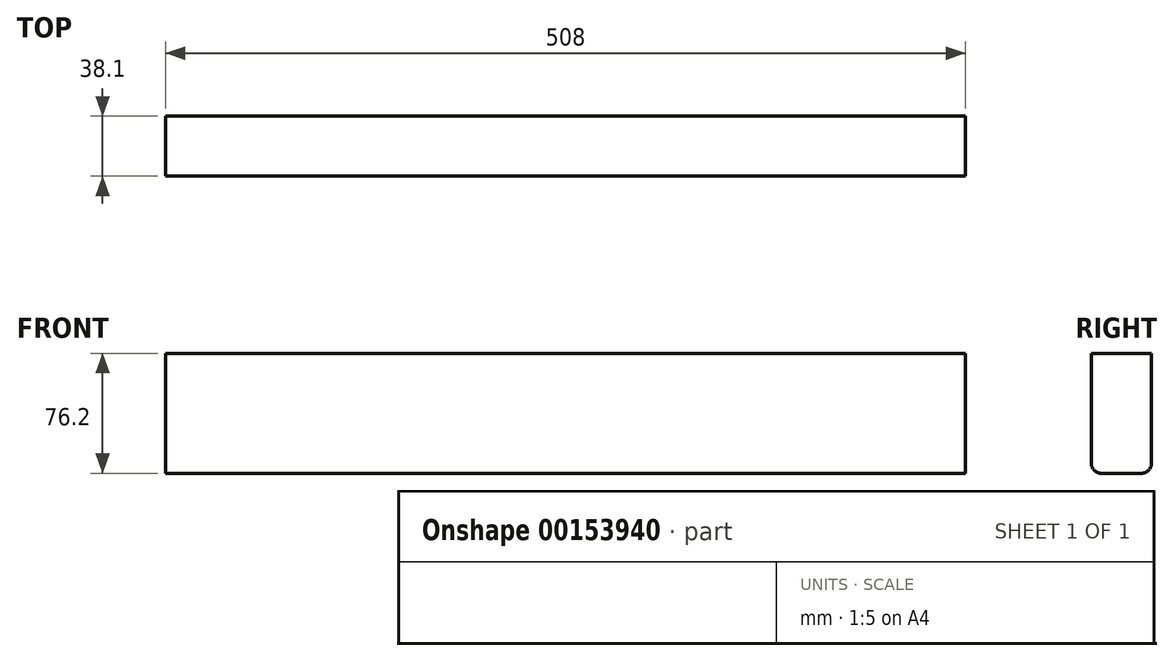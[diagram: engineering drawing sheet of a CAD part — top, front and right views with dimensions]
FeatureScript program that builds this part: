
annotation { "Feature Type Name" : "Feature", "Feature Type Description" : "" }
export const myFeature = defineFeature(function(context is Context, id is Id, definition is map)
    precondition{}
    {
        {
            var Q0;
            Q0=qCreatedBy(makeId("Right.planeOp"),FACE);
            var sketch = newSketch(context, id + "F0", { "sketchPlane" : qUnion([Q0])});
            skLineSegment(sketch, "E0.bottom", {"start": v(31.75, 0) * mm, "end": v(6.35, 0) * mm});
            skLineSegment(sketch, "E0.top", {"start": v(38.1, 76.2) * mm, "end": v(0, 76.2) * mm});
            skLineSegment(sketch, "E0.left", {"start": v(38.1, 6.35) * mm, "end": v(38.1, 76.2) * mm});
            skLineSegment(sketch, "E0.right", {"start": v(0, 6.35) * mm, "end": v(0, 76.2) * mm});
            skPoint(sketch, "E0.middle", {"position": v(0, 0) * mm});
            skArc(sketch, "E1.filletArc", {"start": v(0, 6.35) * mm, "mid": v(1.86, 1.86) * mm, "end": v(6.35, 0) * mm});
            skPoint(sketch, "E2.visualSharp", {"position": v(38.1, 0) * mm});
            skArc(sketch, "E2.filletArc", {"start": v(31.75, 0) * mm, "mid": v(36.24, 1.86) * mm, "end": v(38.1, 6.35) * mm});
            skSolve(sketch);
        }
        {
            var Q0;
            Q0=makeQuery(id+"F0.imprint","IMPRINT",FACE,{"disambiguationData":[TD([[makeQuery(id+"F0.imprint","IMPRINT",EDGE,{"derivedFrom":sQuery(id+"F0.wireOp",EDGE,"E0.bottom")}),-1.0]])]});
            extrude(context, id + "F1", {"entities" : qUnion([Q0]), "endBound" : BoundingType.SYMMETRIC, "depth" : 508 * mm});
        }
    });
